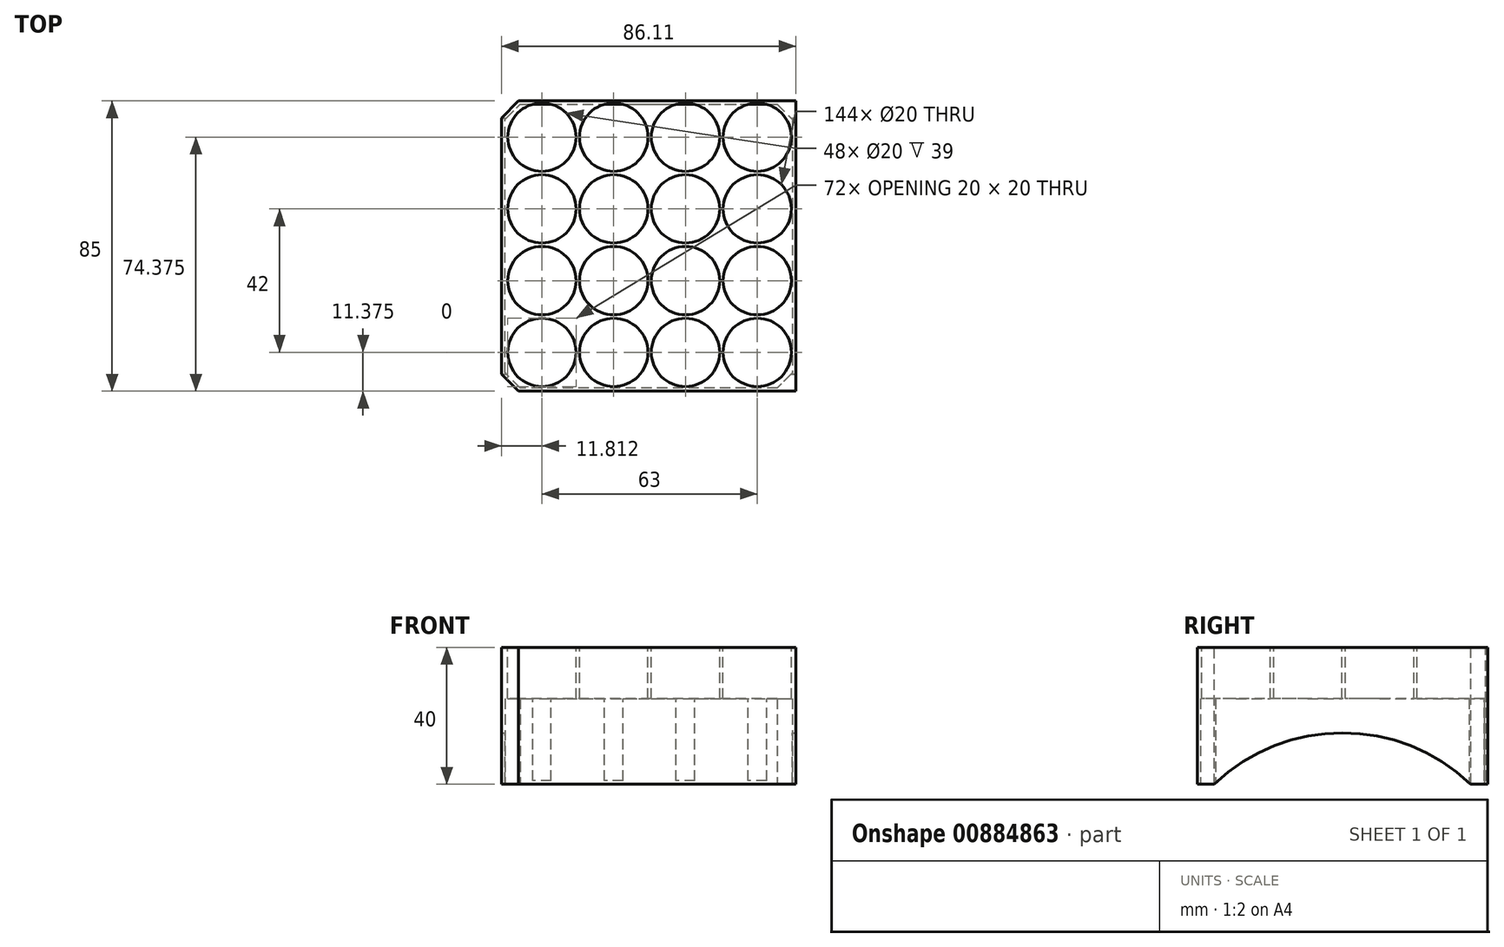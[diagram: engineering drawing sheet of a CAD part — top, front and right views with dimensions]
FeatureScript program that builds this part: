
annotation { "Feature Type Name" : "Feature", "Feature Type Description" : "" }
export const myFeature = defineFeature(function(context is Context, id is Id, definition is map)
    precondition{}
    {
        {
            var Q0;
            Q0=qCreatedBy(makeId("Top.planeOp"),FACE);
            var sketch = newSketch(context, id + "F0", { "sketchPlane" : qUnion([Q0])});
            skLineSegment(sketch, "E0.bottom", {"start": v(-94.5, 42.5) * mm, "end": v(94.5, 42.5) * mm});
            skLineSegment(sketch, "E0.top", {"start": v(-94.5, -42.5) * mm, "end": v(94.5, -42.5) * mm});
            skLineSegment(sketch, "E0.left", {"start": v(-94.5, 42.5) * mm, "end": v(-94.5, -42.5) * mm});
            skLineSegment(sketch, "E0.right", {"start": v(94.5, 42.5) * mm, "end": v(94.5, -42.5) * mm});
            skPoint(sketch, "E0.middle", {"position": v(0, 0) * mm});
            skSolve(sketch);
        }
        {
            var Q0;
            Q0=makeQuery(id+"F0.imprint","IMPRINT",FACE,{"disambiguationData":[TD([[makeQuery(id+"F0.imprint","IMPRINT",EDGE,{"derivedFrom":sQuery(id+"F0.wireOp",EDGE,"E0.bottom")}),-1.0]])]});
            extrude(context, id + "F1", {"entities" : qUnion([Q0]), "depth" : 40 * mm, "offsetDistance" : 25 * mm});
        }
        {
            var Q0;
            Q0=makeQuery(id+"F1.opExtrude","CAP_FACE",FACE,{"disambiguationData":[OSD([sQuery(id+"F0.wireOp",EDGE,"E0.bottom"),sQuery(id+"F0.wireOp",EDGE,"E0.top"),sQuery(id+"F0.wireOp",EDGE,"E0.left"),sQuery(id+"F0.wireOp",EDGE,"E0.right")])],"isStart":false});
            var sketch = newSketch(context, id + "F2", { "sketchPlane" : qUnion([Q0])});
            skLineSegment(sketch, "E1", {"start": v(-94.5, 0) * mm, "end": v(94.5, 0) * mm, "construction": true});
            skLineSegment(sketch, "E2", {"start": v(0, 42.5) * mm, "end": v(0, -42.5) * mm, "construction": true});
            skLineSegment(sketch, "E3", {"start": v(0, 42.5) * mm, "end": v(-94.5, 0) * mm, "construction": true});
            skLineSegment(sketch, "E4", {"start": v(-47.25, 21.25) * mm, "end": v(-94.5, 21.25) * mm, "construction": true});
            skLineSegment(sketch, "E5", {"start": v(-94.5, 21.25) * mm, "end": v(-47.25, 21.25) * mm, "construction": true});
            skLineSegment(sketch, "E6", {"start": v(-47.25, 21.25) * mm, "end": v(94.5, 21.25) * mm, "construction": true});
            skLineSegment(sketch, "E7", {"start": v(-94.5, 42.5) * mm, "end": v(-47.25, 21.25) * mm, "construction": true});
            skLineSegment(sketch, "E8", {"start": v(-70.88, 31.87) * mm, "end": v(-94.5, 31.87) * mm, "construction": true});
            skLineSegment(sketch, "E9", {"start": v(-47.25, 21.25) * mm, "end": v(-94.5, 0) * mm, "construction": true});
            skLineSegment(sketch, "E10", {"start": v(-70.88, 10.63) * mm, "end": v(-94.5, 10.63) * mm, "construction": true});
            skLineSegment(sketch, "E11", {"start": v(-94.5, 10.63) * mm, "end": v(0, 10.63) * mm, "construction": true});
            skLineSegment(sketch, "E12", {"start": v(0, 10.63) * mm, "end": v(94.5, 10.63) * mm, "construction": true});
            skLineSegment(sketch, "E13", {"start": v(-70.88, 31.88) * mm, "end": v(94.5, 31.88) * mm, "construction": true});
            skLineSegment(sketch, "E14", {"start": v(0, 0) * mm, "end": v(-94.5, -42.5) * mm, "construction": true});
            skLineSegment(sketch, "E15", {"start": v(-94.5, 0) * mm, "end": v(-47.25, -21.25) * mm, "construction": true});
            skLineSegment(sketch, "E16", {"start": v(-94.5, -21.25) * mm, "end": v(94.5, -21.25) * mm, "construction": true});
            skLineSegment(sketch, "E17", {"start": v(-94.5, -10.62) * mm, "end": v(94.5, -10.62) * mm, "construction": true});
            skPoint(sketch, "E17.startSnap0", {"position": v(-70.88, -10.62) * mm});
            skLineSegment(sketch, "E18", {"start": v(-47.25, -21.25) * mm, "end": v(-94.5, -42.5) * mm, "construction": true});
            skLineSegment(sketch, "E19", {"start": v(-94.5, -31.88) * mm, "end": v(94.5, -31.88) * mm, "construction": true});
            skPoint(sketch, "E19.startSnap0", {"position": v(-70.88, -31.88) * mm});
            skCircle(sketch, "E20", {"center": v(-82.69, 31.87) * mm, "radius": 10 * mm});
            skCircle(sketch, "E21.0.1.0", {"center": v(-82.69, 10.87) * mm, "radius": 10 * mm});
            skCircle(sketch, "E21.0.2.0", {"center": v(-82.69, -10.13) * mm, "radius": 10 * mm});
            skCircle(sketch, "E21.0.3.0", {"center": v(-82.69, -31.13) * mm, "radius": 10 * mm});
            skCircle(sketch, "E21.1.0.0", {"center": v(-61.69, 31.87) * mm, "radius": 10 * mm});
            skCircle(sketch, "E21.1.1.0", {"center": v(-61.69, 10.87) * mm, "radius": 10 * mm});
            skCircle(sketch, "E21.1.2.0", {"center": v(-61.69, -10.13) * mm, "radius": 10 * mm});
            skCircle(sketch, "E21.1.3.0", {"center": v(-61.69, -31.13) * mm, "radius": 10 * mm});
            skCircle(sketch, "E21.2.0.0", {"center": v(-40.69, 31.87) * mm, "radius": 10 * mm});
            skCircle(sketch, "E21.2.1.0", {"center": v(-40.69, 10.87) * mm, "radius": 10 * mm});
            skCircle(sketch, "E21.2.2.0", {"center": v(-40.69, -10.13) * mm, "radius": 10 * mm});
            skCircle(sketch, "E21.2.3.0", {"center": v(-40.69, -31.13) * mm, "radius": 10 * mm});
            skCircle(sketch, "E21.3.0.0", {"center": v(-19.69, 31.87) * mm, "radius": 10 * mm});
            skCircle(sketch, "E21.3.1.0", {"center": v(-19.69, 10.87) * mm, "radius": 10 * mm});
            skCircle(sketch, "E21.3.2.0", {"center": v(-19.69, -10.13) * mm, "radius": 10 * mm});
            skCircle(sketch, "E21.3.3.0", {"center": v(-19.69, -31.13) * mm, "radius": 10 * mm});
            skLineSegment(sketch, "E21.direction1", {"start": v(-82.69, 31.87) * mm, "end": v(-61.69, 31.87) * mm, "construction": true});
            skLineSegment(sketch, "E21.direction2", {"start": v(-82.69, 31.87) * mm, "end": v(-82.69, 10.87) * mm, "construction": true});
            skSolve(sketch);
        }
        {
            var Q0;
            Q0=makeQuery(id+"F2.imprint","IMPRINT",FACE,{"disambiguationData":[TD([[makeQuery(id+"F2.imprint","IMPRINT",EDGE,{"derivedFrom":sQuery(id+"F2.wireOp",EDGE,"E20")}),1.0]])]});
            var Q1;
            Q1=makeQuery(id+"F2.imprint","IMPRINT",FACE,{"disambiguationData":[TD([[makeQuery(id+"F2.imprint","IMPRINT",EDGE,{"derivedFrom":sQuery(id+"F2.wireOp",EDGE,"E21.1.0.0")}),1.0]])]});
            var Q2;
            Q2=makeQuery(id+"F2.imprint","IMPRINT",FACE,{"disambiguationData":[TD([[makeQuery(id+"F2.imprint","IMPRINT",EDGE,{"derivedFrom":sQuery(id+"F2.wireOp",EDGE,"E21.2.0.0")}),1.0]])]});
            var Q3;
            Q3=makeQuery(id+"F2.imprint","IMPRINT",FACE,{"disambiguationData":[TD([[makeQuery(id+"F2.imprint","IMPRINT",EDGE,{"derivedFrom":sQuery(id+"F2.wireOp",EDGE,"E21.3.0.0")}),1.0]])]});
            var Q4;
            Q4=makeQuery(id+"F2.imprint","IMPRINT",FACE,{"disambiguationData":[TD([[makeQuery(id+"F2.imprint","IMPRINT",EDGE,{"derivedFrom":sQuery(id+"F2.wireOp",EDGE,"E21.4.0.0")}),1.0]])]});
            var Q5;
            Q5=makeQuery(id+"F2.imprint","IMPRINT",FACE,{"disambiguationData":[TD([[makeQuery(id+"F2.imprint","IMPRINT",EDGE,{"derivedFrom":sQuery(id+"F2.wireOp",EDGE,"E21.5.0.0")}),1.0]])]});
            var Q6;
            Q6=makeQuery(id+"F2.imprint","IMPRINT",FACE,{"disambiguationData":[TD([[makeQuery(id+"F2.imprint","IMPRINT",EDGE,{"derivedFrom":sQuery(id+"F2.wireOp",EDGE,"E21.6.0.0")}),1.0]])]});
            var Q7;
            Q7=makeQuery(id+"F2.imprint","IMPRINT",FACE,{"disambiguationData":[TD([[makeQuery(id+"F2.imprint","IMPRINT",EDGE,{"derivedFrom":sQuery(id+"F2.wireOp",EDGE,"E21.7.0.0")}),1.0]])]});
            var Q8;
            Q8=makeQuery(id+"F2.imprint","IMPRINT",FACE,{"disambiguationData":[TD([[makeQuery(id+"F2.imprint","IMPRINT",EDGE,{"derivedFrom":sQuery(id+"F2.wireOp",EDGE,"E21.7.1.0")}),1.0]])]});
            var Q9;
            Q9=makeQuery(id+"F2.imprint","IMPRINT",FACE,{"disambiguationData":[TD([[makeQuery(id+"F2.imprint","IMPRINT",EDGE,{"derivedFrom":sQuery(id+"F2.wireOp",EDGE,"E21.6.1.0")}),1.0]])]});
            var Q10;
            Q10=makeQuery(id+"F2.imprint","IMPRINT",FACE,{"disambiguationData":[TD([[makeQuery(id+"F2.imprint","IMPRINT",EDGE,{"derivedFrom":sQuery(id+"F2.wireOp",EDGE,"E21.5.1.0")}),1.0]])]});
            var Q11;
            Q11=makeQuery(id+"F2.imprint","IMPRINT",FACE,{"disambiguationData":[TD([[makeQuery(id+"F2.imprint","IMPRINT",EDGE,{"derivedFrom":sQuery(id+"F2.wireOp",EDGE,"E21.4.1.0")}),1.0]])]});
            var Q12;
            Q12=makeQuery(id+"F2.imprint","IMPRINT",FACE,{"disambiguationData":[TD([[makeQuery(id+"F2.imprint","IMPRINT",EDGE,{"derivedFrom":sQuery(id+"F2.wireOp",EDGE,"E21.3.1.0")}),1.0]])]});
            var Q13;
            Q13=makeQuery(id+"F2.imprint","IMPRINT",FACE,{"disambiguationData":[TD([[makeQuery(id+"F2.imprint","IMPRINT",EDGE,{"derivedFrom":sQuery(id+"F2.wireOp",EDGE,"E21.2.1.0")}),1.0]])]});
            var Q14;
            Q14=makeQuery(id+"F2.imprint","IMPRINT",FACE,{"disambiguationData":[TD([[makeQuery(id+"F2.imprint","IMPRINT",EDGE,{"derivedFrom":sQuery(id+"F2.wireOp",EDGE,"E21.1.1.0")}),1.0]])]});
            var Q15;
            Q15=makeQuery(id+"F2.imprint","IMPRINT",FACE,{"disambiguationData":[TD([[makeQuery(id+"F2.imprint","IMPRINT",EDGE,{"derivedFrom":sQuery(id+"F2.wireOp",EDGE,"E21.0.1.0")}),1.0]])]});
            var Q16;
            Q16=makeQuery(id+"F2.imprint","IMPRINT",FACE,{"disambiguationData":[TD([[makeQuery(id+"F2.imprint","IMPRINT",EDGE,{"derivedFrom":sQuery(id+"F2.wireOp",EDGE,"E21.0.2.0")}),1.0]])]});
            var Q17;
            Q17=makeQuery(id+"F2.imprint","IMPRINT",FACE,{"disambiguationData":[TD([[makeQuery(id+"F2.imprint","IMPRINT",EDGE,{"derivedFrom":sQuery(id+"F2.wireOp",EDGE,"E21.1.2.0")}),1.0]])]});
            var Q18;
            Q18=makeQuery(id+"F2.imprint","IMPRINT",FACE,{"disambiguationData":[TD([[makeQuery(id+"F2.imprint","IMPRINT",EDGE,{"derivedFrom":sQuery(id+"F2.wireOp",EDGE,"E21.2.2.0")}),1.0]])]});
            var Q19;
            Q19=makeQuery(id+"F2.imprint","IMPRINT",FACE,{"disambiguationData":[TD([[makeQuery(id+"F2.imprint","IMPRINT",EDGE,{"derivedFrom":sQuery(id+"F2.wireOp",EDGE,"E21.3.2.0")}),1.0]])]});
            var Q20;
            Q20=makeQuery(id+"F2.imprint","IMPRINT",FACE,{"disambiguationData":[TD([[makeQuery(id+"F2.imprint","IMPRINT",EDGE,{"derivedFrom":sQuery(id+"F2.wireOp",EDGE,"E21.4.2.0")}),1.0]])]});
            var Q21;
            Q21=makeQuery(id+"F2.imprint","IMPRINT",FACE,{"disambiguationData":[TD([[makeQuery(id+"F2.imprint","IMPRINT",EDGE,{"derivedFrom":sQuery(id+"F2.wireOp",EDGE,"E21.5.2.0")}),1.0]])]});
            var Q22;
            Q22=makeQuery(id+"F2.imprint","IMPRINT",FACE,{"disambiguationData":[TD([[makeQuery(id+"F2.imprint","IMPRINT",EDGE,{"derivedFrom":sQuery(id+"F2.wireOp",EDGE,"E21.6.2.0")}),1.0]])]});
            var Q23;
            Q23=makeQuery(id+"F2.imprint","IMPRINT",FACE,{"disambiguationData":[TD([[makeQuery(id+"F2.imprint","IMPRINT",EDGE,{"derivedFrom":sQuery(id+"F2.wireOp",EDGE,"E21.7.2.0")}),1.0]])]});
            var Q24;
            Q24=makeQuery(id+"F2.imprint","IMPRINT",FACE,{"disambiguationData":[TD([[makeQuery(id+"F2.imprint","IMPRINT",EDGE,{"derivedFrom":sQuery(id+"F2.wireOp",EDGE,"E21.7.3.0")}),1.0]])]});
            var Q25;
            Q25=makeQuery(id+"F2.imprint","IMPRINT",FACE,{"disambiguationData":[TD([[makeQuery(id+"F2.imprint","IMPRINT",EDGE,{"derivedFrom":sQuery(id+"F2.wireOp",EDGE,"E21.6.3.0")}),1.0]])]});
            var Q26;
            Q26=makeQuery(id+"F2.imprint","IMPRINT",FACE,{"disambiguationData":[TD([[makeQuery(id+"F2.imprint","IMPRINT",EDGE,{"derivedFrom":sQuery(id+"F2.wireOp",EDGE,"E21.5.3.0")}),1.0]])]});
            var Q27;
            Q27=makeQuery(id+"F2.imprint","IMPRINT",FACE,{"disambiguationData":[TD([[makeQuery(id+"F2.imprint","IMPRINT",EDGE,{"derivedFrom":sQuery(id+"F2.wireOp",EDGE,"E21.4.3.0")}),1.0]])]});
            var Q28;
            Q28=makeQuery(id+"F2.imprint","IMPRINT",FACE,{"disambiguationData":[TD([[makeQuery(id+"F2.imprint","IMPRINT",EDGE,{"derivedFrom":sQuery(id+"F2.wireOp",EDGE,"E21.3.3.0")}),1.0]])]});
            var Q29;
            Q29=makeQuery(id+"F2.imprint","IMPRINT",FACE,{"disambiguationData":[TD([[makeQuery(id+"F2.imprint","IMPRINT",EDGE,{"derivedFrom":sQuery(id+"F2.wireOp",EDGE,"E21.2.3.0")}),1.0]])]});
            var Q30;
            Q30=makeQuery(id+"F2.imprint","IMPRINT",FACE,{"disambiguationData":[TD([[makeQuery(id+"F2.imprint","IMPRINT",EDGE,{"derivedFrom":sQuery(id+"F2.wireOp",EDGE,"E21.1.3.0")}),1.0]])]});
            var Q31;
            Q31=makeQuery(id+"F2.imprint","IMPRINT",FACE,{"disambiguationData":[TD([[makeQuery(id+"F2.imprint","IMPRINT",EDGE,{"derivedFrom":sQuery(id+"F2.wireOp",EDGE,"E21.0.3.0")}),1.0]])]});
            extrude(context, id + "F3", {"entities" : qUnion([Q0, Q1, Q2, Q3, Q4, Q5, Q6, Q7, Q8, Q9, Q10, Q11, Q12, Q13, Q14, Q15, Q16, Q17, Q18, Q19, Q20, Q21, Q22, Q23, Q24, Q25, Q26, Q27, Q28, Q29, Q30, Q31]), "operationType" : NewBodyOperationType.REMOVE, "oppositeDirection" : true, "depth" : 39 * mm, "offsetDistance" : 25 * mm});
        }
        {
            var Q0;
            Q0=makeQuery(id+"F9zTTeWclKvBw9Y_1.opChamfer","SPLIT",FACE,{"disambiguationData":[OD(12.0)],"derivedFrom":makeQuery(id+"F1.opExtrude","CAP_FACE",FACE,{"disambiguationData":[OSD([sQuery(id+"F0.wireOp",EDGE,"E0.bottom"),sQuery(id+"F0.wireOp",EDGE,"E0.top"),sQuery(id+"F0.wireOp",EDGE,"E0.left"),sQuery(id+"F0.wireOp",EDGE,"E0.right")])],"isStart":false})});
            var sketch = newSketch(context, id + "F4", { "sketchPlane" : qUnion([Q0])});
            skLineSegment(sketch, "E22", {"start": v(-8.4, 42.5) * mm, "end": v(-8.4, -42.5) * mm});
            skSolve(sketch);
        }
        {
            var Q0;
            {var subQ0=sQuery(id+"F4.wireOp",EDGE,"E22");Q0=makeQuery(id+"F4.imprint","IMPRINT",FACE,{"disambiguationData":[TD([[makeQuery(id+"F4.imprint","IMPRINT",EDGE,{"derivedFrom":subQ0}),1.0]])]});}
            extrude(context, id + "F5", {"entities" : qUnion([Q0]), "operationType" : NewBodyOperationType.REMOVE, "endBound" : BoundingType.THROUGH_ALL, "oppositeDirection" : true, "depth" : 25 * mm, "offsetDistance" : 25 * mm});
        }
        {
            var Q0;
            Q0=makeQuery(id+"F1.opExtrude","SWEPT_EDGE",EDGE,{"disambiguationData":[OSD([sQuery(id+"F0.wireOp",EDGE,"E0.bottom"),sQuery(id+"F0.wireOp",EDGE,"E0.left")])]});
            var Q1;
            Q1=makeQuery(id+"F5.boolean.opBoolean","COPY",EDGE,{"derivedFrom":makeQuery(id+"F5.opExtrude","SWEPT_EDGE",EDGE,{"disambiguationData":[OSD([sQuery(id+"F0.wireOp",EDGE,"E0.bottom"),sQuery(id+"F4.wireOp",EDGE,"E22")])]})});
            var Q2;
            Q2=makeQuery(id+"F5.boolean.opBoolean","COPY",EDGE,{"derivedFrom":makeQuery(id+"F5.opExtrude","SWEPT_EDGE",EDGE,{"disambiguationData":[OSD([sQuery(id+"F0.wireOp",EDGE,"E0.top"),sQuery(id+"F4.wireOp",EDGE,"E22")])]})});
            var Q3;
            Q3=makeQuery(id+"F1.opExtrude","SWEPT_EDGE",EDGE,{"disambiguationData":[OSD([sQuery(id+"F0.wireOp",EDGE,"E0.top"),sQuery(id+"F0.wireOp",EDGE,"E0.left")])]});
            chamfer(context, id + "F6", {"entities" : qUnion([Q0, Q1, Q2, Q3]), "width" : 5 * mm, "tangentPropagation" : true});
        }
        {
            var Q0;
            Q0=makeQuery(id+"F1.opExtrude","CAP_FACE",FACE,{"disambiguationData":[OSD([sQuery(id+"F0.wireOp",EDGE,"E0.bottom"),sQuery(id+"F0.wireOp",EDGE,"E0.top"),sQuery(id+"F0.wireOp",EDGE,"E0.left"),sQuery(id+"F0.wireOp",EDGE,"E0.right")])],"isStart":true});
            var sketch = newSketch(context, id + "F7", { "sketchPlane" : qUnion([Q0])});
            skLineSegment(sketch, "E23.0", {"start": v(-9.4, 37.09) * mm, "end": v(-13.8, 41.5) * mm});
            skLineSegment(sketch, "E23.1", {"start": v(-9.4, -37.09) * mm, "end": v(-9.4, 37.09) * mm});
            skLineSegment(sketch, "E23.2", {"start": v(-13.8, 41.5) * mm, "end": v(-89.09, 41.5) * mm});
            skLineSegment(sketch, "E23.3", {"start": v(-13.8, -41.5) * mm, "end": v(-9.4, -37.09) * mm});
            skLineSegment(sketch, "E23.4", {"start": v(-89.09, 41.5) * mm, "end": v(-93.5, 37.09) * mm});
            skLineSegment(sketch, "E23.5", {"start": v(-93.5, 37.09) * mm, "end": v(-93.5, -37.09) * mm});
            skLineSegment(sketch, "E23.6", {"start": v(-93.5, -37.09) * mm, "end": v(-89.09, -41.5) * mm});
            skLineSegment(sketch, "E23.7", {"start": v(-89.09, -41.5) * mm, "end": v(-13.8, -41.5) * mm});
            skSolve(sketch);
        }
        {
            var Q0;
            Q0=makeQuery(id+"F7.imprint","IMPRINT",FACE,{"disambiguationData":[TD([[makeQuery(id+"F7.imprint","IMPRINT",EDGE,{"derivedFrom":sQuery(id+"F7.wireOp",EDGE,"E23.0")}),1.0]])]});
            extrude(context, id + "F8", {"entities" : qUnion([Q0]), "operationType" : NewBodyOperationType.REMOVE, "oppositeDirection" : true, "depth" : 25 * mm, "offsetDistance" : 25 * mm});
        }
        {
            var Q0;
            Q0=makeQuery(id+"F5.boolean.opBoolean","COPY",FACE,{"derivedFrom":makeQuery(id+"F5.opExtrude","SWEPT_FACE",FACE,{"disambiguationData":[OSD([sQuery(id+"F4.wireOp",EDGE,"E22")])]})});
            var sketch = newSketch(context, id + "F9", { "sketchPlane" : qUnion([Q0])});
            skArc(sketch, "E24", {"start": v(37.5, 0) * mm, "mid": v(0, 15) * mm, "end": v(-37.5, 0) * mm});
            skSolve(sketch);
        }
        {
            var Q0;
            Q0=makeQuery(id+"F9.imprint","IMPRINT",FACE,{"disambiguationData":[TD([[makeQuery(id+"F9.imprint","IMPRINT",EDGE,{"derivedFrom":sQuery(id+"F9.wireOp",EDGE,"E24")}),1.0]])]});
            extrude(context, id + "F10", {"entities" : qUnion([Q0]), "operationType" : NewBodyOperationType.REMOVE, "endBound" : BoundingType.THROUGH_ALL, "oppositeDirection" : true, "depth" : 25 * mm, "offsetDistance" : 25 * mm});
        }
    });
